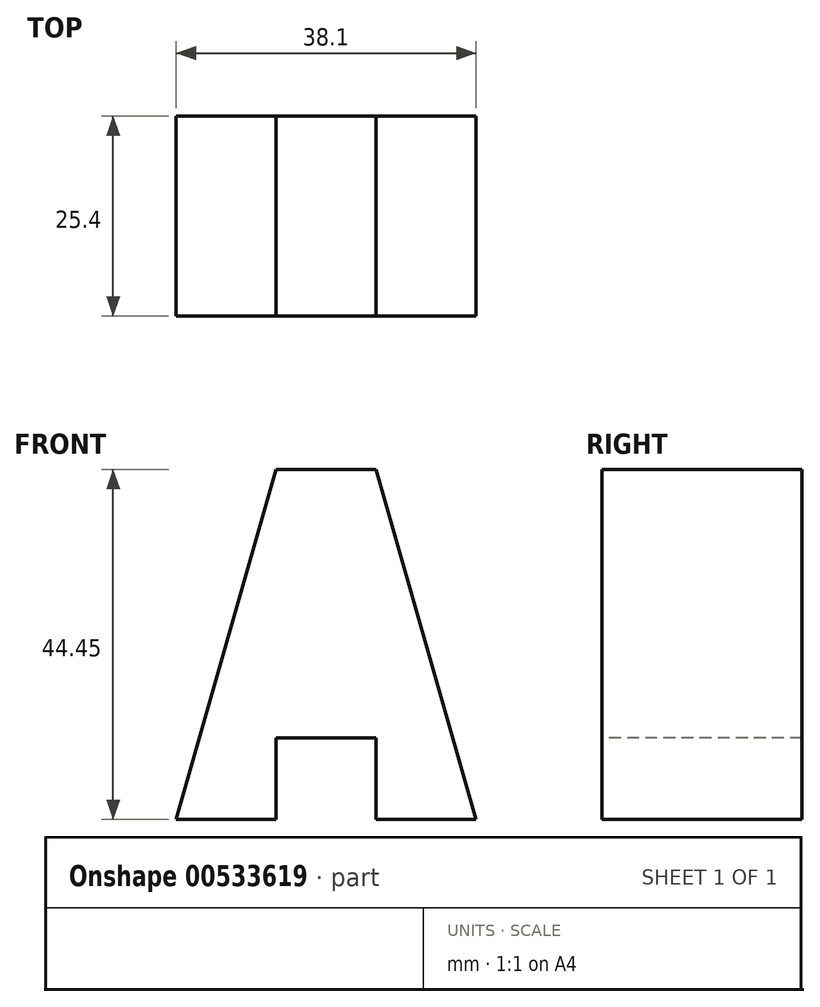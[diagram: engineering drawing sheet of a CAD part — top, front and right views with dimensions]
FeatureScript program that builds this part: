
annotation { "Feature Type Name" : "Feature", "Feature Type Description" : "" }
export const myFeature = defineFeature(function(context is Context, id is Id, definition is map)
    precondition{}
    {
        {
            var Q0;
            Q0=qCreatedBy(makeId("Front.planeOp"),FACE);
            var sketch = newSketch(context, id + "F0", { "sketchPlane" : qUnion([Q0])});
            skLineSegment(sketch, "E0", {"start": v(-68.02, 54.37) * mm, "end": v(-68.02, 9.92) * mm});
            skLineSegment(sketch, "E1", {"start": v(-68.02, 9.92) * mm, "end": v(-29.92, 9.92) * mm});
            skLineSegment(sketch, "E2", {"start": v(-29.92, 9.92) * mm, "end": v(-29.92, 54.37) * mm});
            skLineSegment(sketch, "E3", {"start": v(-29.92, 54.37) * mm, "end": v(-68.02, 54.37) * mm});
            skSolve(sketch);
        }
        {
            var Q0;
            Q0 = qSketchRegion(id + "F0", true);
            extrude(context, id + "F1", {"entities" : qUnion([Q0]), "depth" : 25.4 * mm, "offsetDistance" : 25.4 * mm});
        }
        {
            var Q0;
            Q0=makeQuery(id+"F1.opExtrude","CAP_FACE",FACE,{"disambiguationData":[OSD([sQuery(id+"F0.wireOp",EDGE,"E0"),sQuery(id+"F0.wireOp",EDGE,"E1"),sQuery(id+"F0.wireOp",EDGE,"E2"),sQuery(id+"F0.wireOp",EDGE,"E3")])],"isStart":false});
            var sketch = newSketch(context, id + "F2", { "sketchPlane" : qUnion([Q0])});
            skLineSegment(sketch, "E4", {"start": v(-55.32, 9.92) * mm, "end": v(-55.32, 20.29) * mm});
            skLineSegment(sketch, "E5", {"start": v(-55.32, 20.29) * mm, "end": v(-42.62, 20.29) * mm});
            skLineSegment(sketch, "E6", {"start": v(-42.62, 20.29) * mm, "end": v(-42.62, 9.92) * mm});
            skSolve(sketch);
        }
        {
            var Q0;
            Q0 = qSketchRegion(id + "F2", true);
            var Q1;
            {var subQ0=sQuery(id+"F2.wireOp",EDGE,"E4");Q1=makeQuery(id+"F2.imprint","IMPRINT",FACE,{"disambiguationData":[TD([[makeQuery(id+"F2.imprint","IMPRINT",EDGE,{"derivedFrom":subQ0}),-1.0]])]});}
            extrude(context, id + "F3", {"entities" : qUnion([Q0, Q1]), "operationType" : NewBodyOperationType.REMOVE, "endBound" : BoundingType.THROUGH_ALL, "oppositeDirection" : true, "depth" : 25.4 * mm, "offsetDistance" : 25.4 * mm});
        }
        {
            var Q0;
            Q0=makeQuery(id+"F1.opExtrude","CAP_FACE",FACE,{"disambiguationData":[OSD([sQuery(id+"F0.wireOp",EDGE,"E0"),sQuery(id+"F0.wireOp",EDGE,"E1"),sQuery(id+"F0.wireOp",EDGE,"E2"),sQuery(id+"F0.wireOp",EDGE,"E3")])],"isStart":false});
            var sketch = newSketch(context, id + "F4", { "sketchPlane" : qUnion([Q0])});
            skLineSegment(sketch, "E7", {"start": v(-68.02, 9.92) * mm, "end": v(-55.32, 54.37) * mm});
            skLineSegment(sketch, "E8", {"start": v(-29.92, 9.92) * mm, "end": v(-42.62, 54.37) * mm});
            skSolve(sketch);
        }
        {
            var Q0;
            Q0 = qSketchRegion(id + "F4", true);
            var Q1;
            {var subQ0=sQuery(id+"F4.wireOp",EDGE,"E7");Q1=makeQuery(id+"F4.imprint","IMPRINT",FACE,{"disambiguationData":[TD([[makeQuery(id+"F4.imprint","IMPRINT",EDGE,{"derivedFrom":subQ0}),1.0]])]});}
            var Q2;
            {var subQ0=sQuery(id+"F4.wireOp",EDGE,"E8");Q2=makeQuery(id+"F4.imprint","IMPRINT",FACE,{"disambiguationData":[TD([[makeQuery(id+"F4.imprint","IMPRINT",EDGE,{"derivedFrom":subQ0}),-1.0]])]});}
            extrude(context, id + "F5", {"entities" : qUnion([Q0, Q1, Q2]), "operationType" : NewBodyOperationType.REMOVE, "endBound" : BoundingType.THROUGH_ALL, "oppositeDirection" : true, "depth" : 25.4 * mm, "offsetDistance" : 25.4 * mm});
        }
    });
